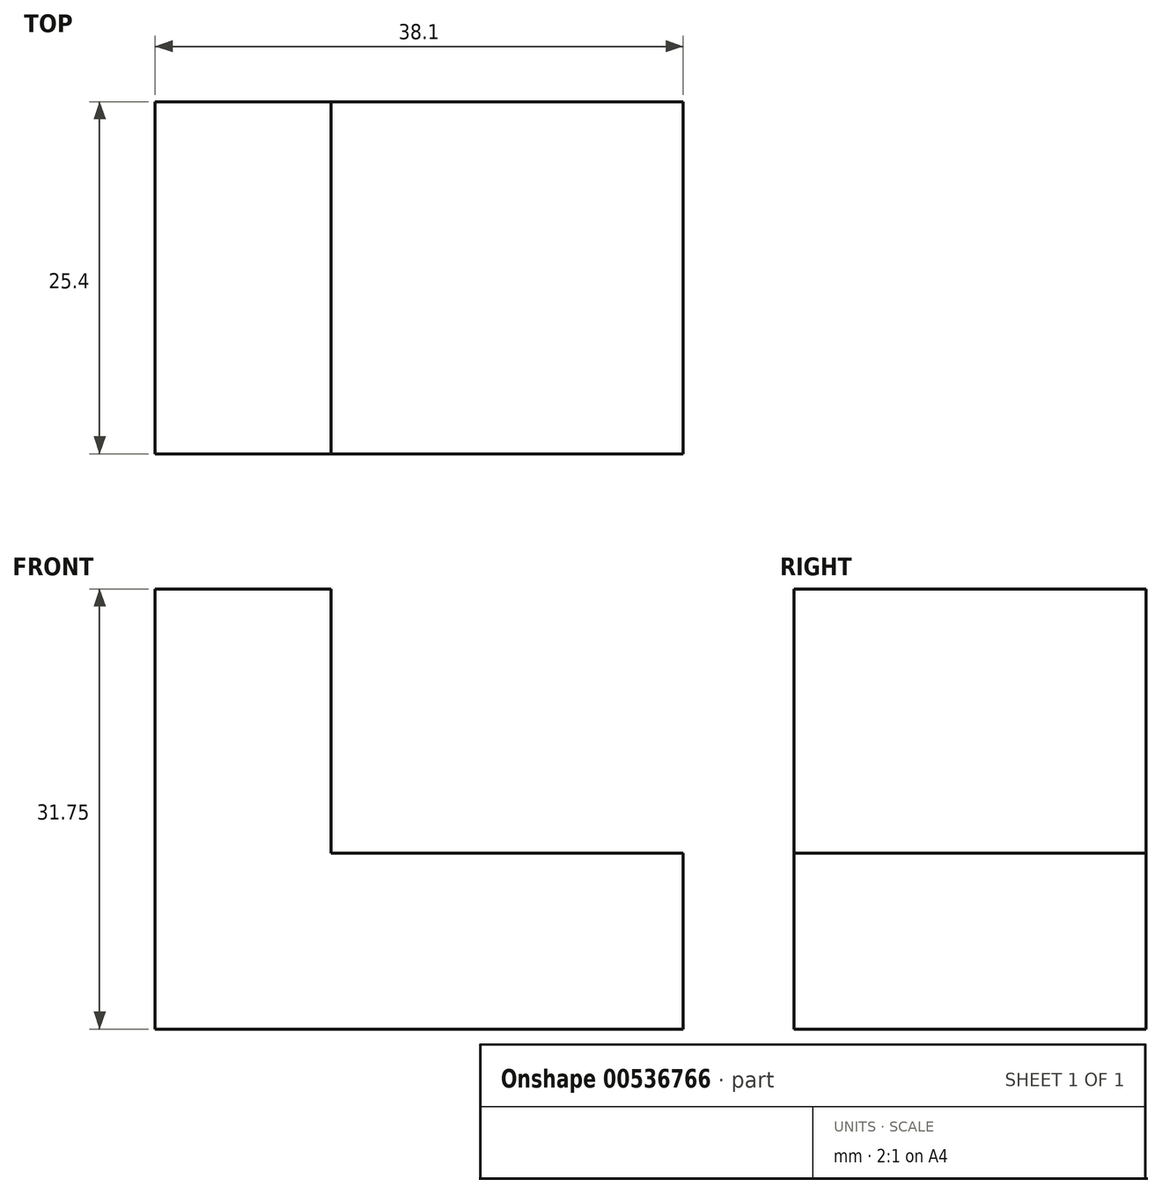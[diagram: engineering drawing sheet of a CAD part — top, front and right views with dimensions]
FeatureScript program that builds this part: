
annotation { "Feature Type Name" : "Feature", "Feature Type Description" : "" }
export const myFeature = defineFeature(function(context is Context, id is Id, definition is map)
    precondition{}
    {
        {
            var Q0;
            Q0=qCreatedBy(makeId("Front.planeOp"),FACE);
            var sketch = newSketch(context, id + "F0", { "sketchPlane" : qUnion([Q0])});
            skLineSegment(sketch, "E0", {"start": v(-62.75, 60.5) * mm, "end": v(-62.75, 28.75) * mm});
            skLineSegment(sketch, "E1", {"start": v(-62.75, 28.75) * mm, "end": v(-24.65, 28.75) * mm});
            skLineSegment(sketch, "E2", {"start": v(-24.65, 28.75) * mm, "end": v(-24.65, 41.45) * mm});
            skLineSegment(sketch, "E3", {"start": v(-24.65, 41.45) * mm, "end": v(-50.05, 41.45) * mm});
            skLineSegment(sketch, "E4", {"start": v(-50.05, 41.45) * mm, "end": v(-50.05, 60.5) * mm});
            skLineSegment(sketch, "E5", {"start": v(-50.05, 60.5) * mm, "end": v(-62.75, 60.5) * mm});
            skSolve(sketch);
        }
        {
            var Q0;
            Q0 = qSketchRegion(id + "F0", true);
            extrude(context, id + "F1", {"entities" : qUnion([Q0]), "depth" : 25.4 * mm, "offsetDistance" : 25.4 * mm});
        }
    });
